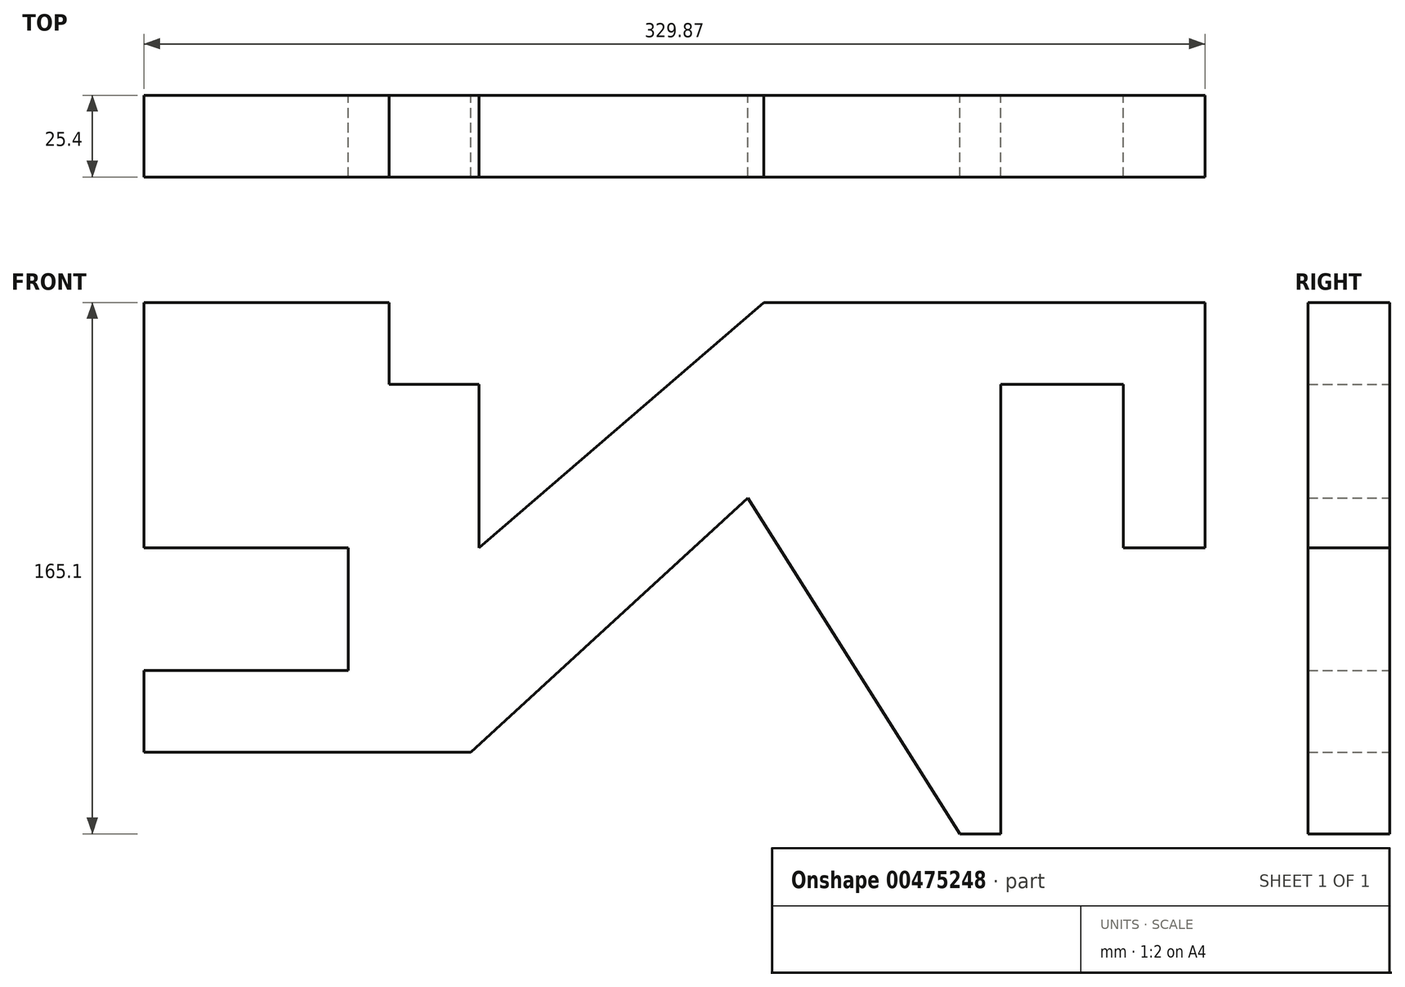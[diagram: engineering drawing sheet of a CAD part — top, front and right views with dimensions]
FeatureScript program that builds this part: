
annotation { "Feature Type Name" : "Feature", "Feature Type Description" : "" }
export const myFeature = defineFeature(function(context is Context, id is Id, definition is map)
    precondition{}
    {
        {
            var Q0;
            Q0=qCreatedBy(makeId("Front.planeOp"),FACE);
            var sketch = newSketch(context, id + "F0", { "sketchPlane" : qUnion([Q0])});
            skLineSegment(sketch, "E0", {"start": v(0, 0) * mm, "end": v(0, -50.8) * mm});
            skLineSegment(sketch, "E1", {"start": v(0, -50.8) * mm, "end": v(63.5, -50.8) * mm});
            skLineSegment(sketch, "E2", {"start": v(63.5, -50.8) * mm, "end": v(63.5, -88.9) * mm});
            skLineSegment(sketch, "E3", {"start": v(63.5, -88.9) * mm, "end": v(0, -88.9) * mm});
            skLineSegment(sketch, "E4", {"start": v(0, -88.9) * mm, "end": v(0, -114.3) * mm});
            skLineSegment(sketch, "E5", {"start": v(0, -114.3) * mm, "end": v(101.6, -114.3) * mm});
            skLineSegment(sketch, "E6", {"start": v(101.6, -114.3) * mm, "end": v(187.7, -35.32) * mm});
            skLineSegment(sketch, "E7", {"start": v(187.7, -35.32) * mm, "end": v(253.67, -139.7) * mm});
            skLineSegment(sketch, "E8", {"start": v(253.67, -139.7) * mm, "end": v(266.37, -139.7) * mm});
            skLineSegment(sketch, "E9", {"start": v(266.37, -139.7) * mm, "end": v(266.37, 0) * mm});
            skLineSegment(sketch, "E10", {"start": v(266.37, 0) * mm, "end": v(304.47, 0) * mm});
            skLineSegment(sketch, "E11", {"start": v(304.47, 0) * mm, "end": v(304.47, -50.8) * mm});
            skLineSegment(sketch, "E12", {"start": v(304.47, -50.8) * mm, "end": v(329.87, -50.8) * mm});
            skLineSegment(sketch, "E13", {"start": v(329.87, -50.8) * mm, "end": v(329.87, 0) * mm});
            skLineSegment(sketch, "E14", {"start": v(329.87, 0) * mm, "end": v(329.87, 25.4) * mm});
            skLineSegment(sketch, "E15", {"start": v(329.87, 25.4) * mm, "end": v(192.71, 25.4) * mm});
            skLineSegment(sketch, "E16", {"start": v(192.71, 25.4) * mm, "end": v(104.14, -50.8) * mm});
            skLineSegment(sketch, "E17", {"start": v(104.14, -50.8) * mm, "end": v(104.14, 0) * mm});
            skLineSegment(sketch, "E18", {"start": v(104.14, 0) * mm, "end": v(76.2, 0) * mm});
            skLineSegment(sketch, "E19", {"start": v(76.2, 0) * mm, "end": v(76.2, 25.4) * mm});
            skLineSegment(sketch, "E20", {"start": v(76.2, 25.4) * mm, "end": v(0, 25.4) * mm});
            skLineSegment(sketch, "E21", {"start": v(0, 25.4) * mm, "end": v(0, 0) * mm});
            skSolve(sketch);
        }
        {
            var Q0;
            Q0 = qSketchRegion(id + "F0", true);
            extrude(context, id + "F1", {"entities" : qUnion([Q0]), "depth" : 25.4 * mm});
        }
    });
